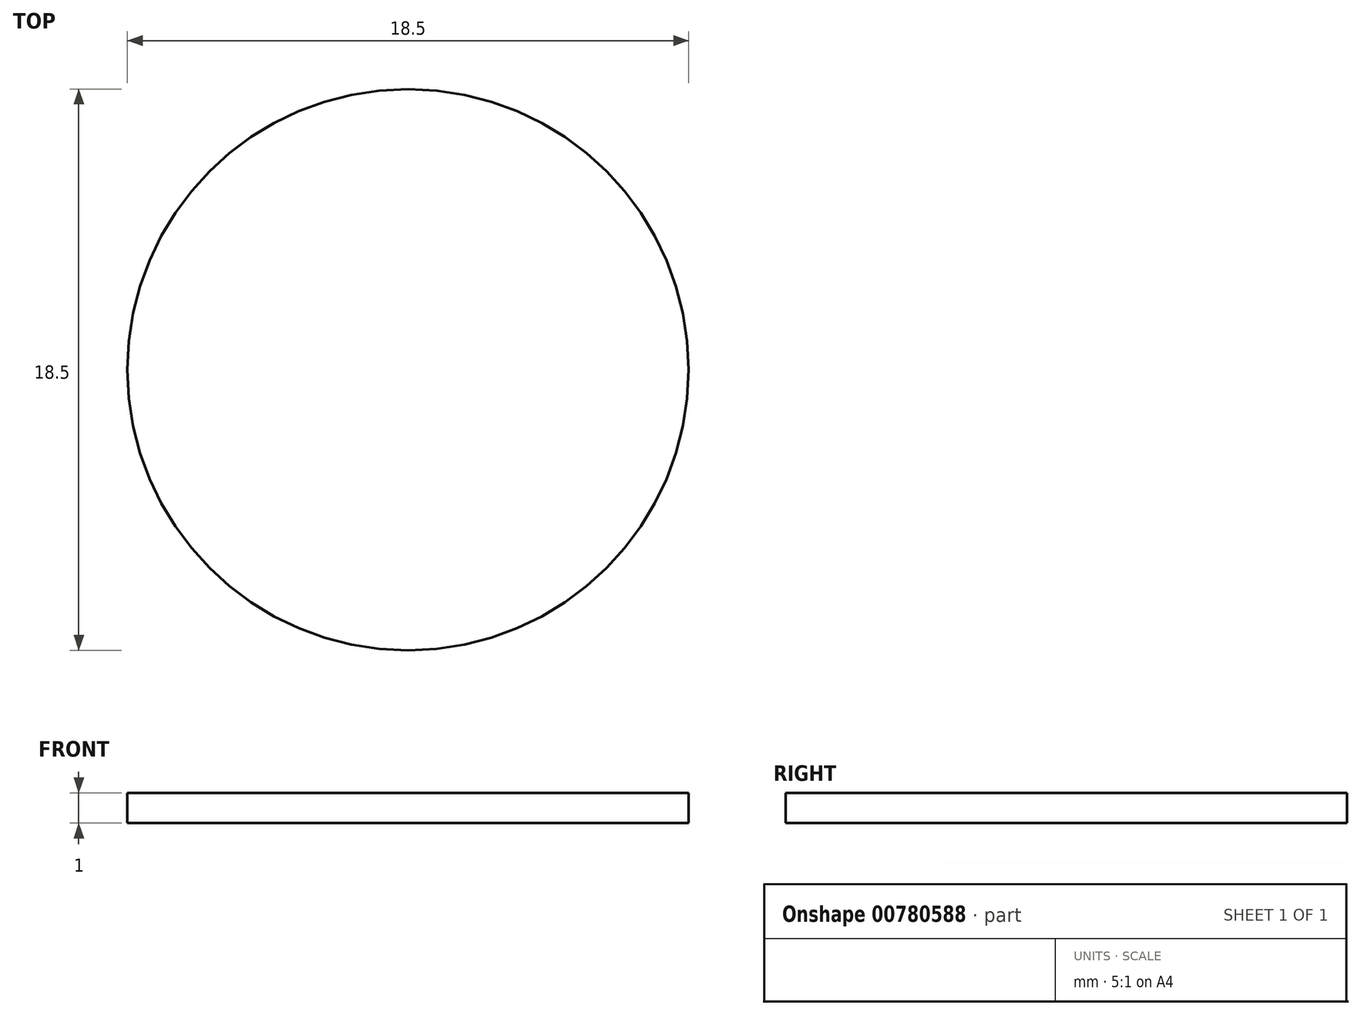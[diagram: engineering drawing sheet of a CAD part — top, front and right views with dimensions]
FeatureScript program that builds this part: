
annotation { "Feature Type Name" : "Feature", "Feature Type Description" : "" }
export const myFeature = defineFeature(function(context is Context, id is Id, definition is map)
    precondition{}
    {
        {
            var Q0;
            Q0=qCreatedBy(makeId("Top.planeOp"),FACE);
            var sketch = newSketch(context, id + "F0", { "sketchPlane" : qUnion([Q0])});
            skCircle(sketch, "E0", {"center": v(0, 0) * mm, "radius": 9.25 * mm});
            skSolve(sketch);
        }
        {
            var Q0;
            Q0 = qSketchRegion(id + "F0", true);
            extrude(context, id + "F1", {"entities" : qUnion([Q0]), "depth" : 1 * mm, "offsetDistance" : 25 * mm});
        }
    });
